# Revit family: Invisiline_диффузор_щелевой_AESTH.S_50+BOX.S_SUP
name_source: partatom
category: Воздухораспределители
units: mm (PartAtom-declared; Revit-internal decimal feet)

## family parameters
Всегда вертикально = Да
Заголовок OmniClass = Diffusers, Registers, and Grilles
На основе рабочей плоскости = Нет
Номер OmniClass = 23.75.70.21.27.11
Общий = Нет
При загрузке вырезать с полостями = Нет
Размер круглого соединителя = Использовать диаметр
Тип детали = Нормальный
Точка расчета площади = Да

## types (4) — shared parameters
2_w = 50 мм
5_2 = 5 : 2 – Самостоятельный диффузор - элемент + 2 торцевые пластины с двух 2 сторон (+3 мм)
5_A = 5 : A – пустой элемент
5_B = 5 : B – торцевая пластина с одной стороны (+1.5 мм)
5_C = 5 : C – коннекторы с одной стороны и торцевая пластина с другой (+1.5 мм)
5_D = 5 : D – коннекторы и разделитель с одной стороны (+1.5 мм), торцевая пластина с другой (+1.5 мм)
5_E = 5 : E – коннекторы с одной стороны
5_F = 5 : F – коннекторы и разделитель с одной стороны (+1.5 мм)
5_G = 5 : G – коннекторы с двух сторон
5_H = 5 : H – коннекторы и разделители (+3 мм) с двух сторон
5_I = 5 : I – коннекторы с одной стороны и коннекторы с разделителем с другой (+1.5 мм)
ADSK_Версия семейства = Ver. 3 2025-11
ADSK_Количество = 1
ADSK_Материал = INVISILINE_Условный_Белый
B = 150 мм
Con_Vis = Нет
Con_h1 = 85 мм
D = 160 мм
K_A = 7.19
K_B = -6.1
LT = AESTH_50
URL = www.invisiline.ru
Wb1 = 190 мм
h = 74 мм
Изготовитель = Invisiline
КСД_H = 259 мм
КСД_H_2 = 174 мм
КСД_W = 190 мм
Шаг приращения длины = 5 мм

## per-type parameters (varying)
| type | 6_КСД | Vr_FRNT_Vis | Vr_STD_Vis | КСД_H_FRNT |
| AESTH.S-50-*-*-* + BOX.S-50-*-STD | 1 | Нет | Да | 259 мм |
| AESTH.S-50-*-*-* + BOX.S-50-*-CUST | 0 | Нет | Нет | 259 мм |
| AESTH.S-50-*-*-* + BOX.S-50-*-FRNT | 2 | Да | Нет | 309 мм |
| AESTH.S-50-*-*-* + BOX.S-50-*-NULL | 3 | Нет | Нет | 259 мм |

## geometry (parser evidence)
native form markers: Sweep x3
no freeform markers — native parametric forms only
